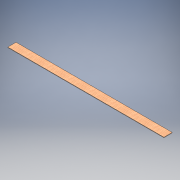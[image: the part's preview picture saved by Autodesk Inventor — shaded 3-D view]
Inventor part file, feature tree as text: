
AUTODESK INVENTOR PART (.ipt)
format: ipt  version: 2018 (Build 220112000, 112)  size: 119,808 bytes
history: native  units: mm
features: other x1, extrude x1, sketch x1
ambient origin geometry x8: Origin, YZ Plane, XZ Plane, XY Plane, X Axis, Y Axis, Z Axis, Center Point
bodies: Solid1 (feature_tree)
feature tree (3):
  parser-record x1  (decoder bookkeeping rows leaked as tree rows — omitted from the tree; the rows remain in map.json)
  extrude  "Extrusion1"  Depth=100.0mm
  sketch  "Sketch1"  dims[d0=1884.0mm d1=100.0mm d2=6.0mm d3=0.0mm]
note: 1 file-system path scrubbed to <path> (originals preserved in map.json)
